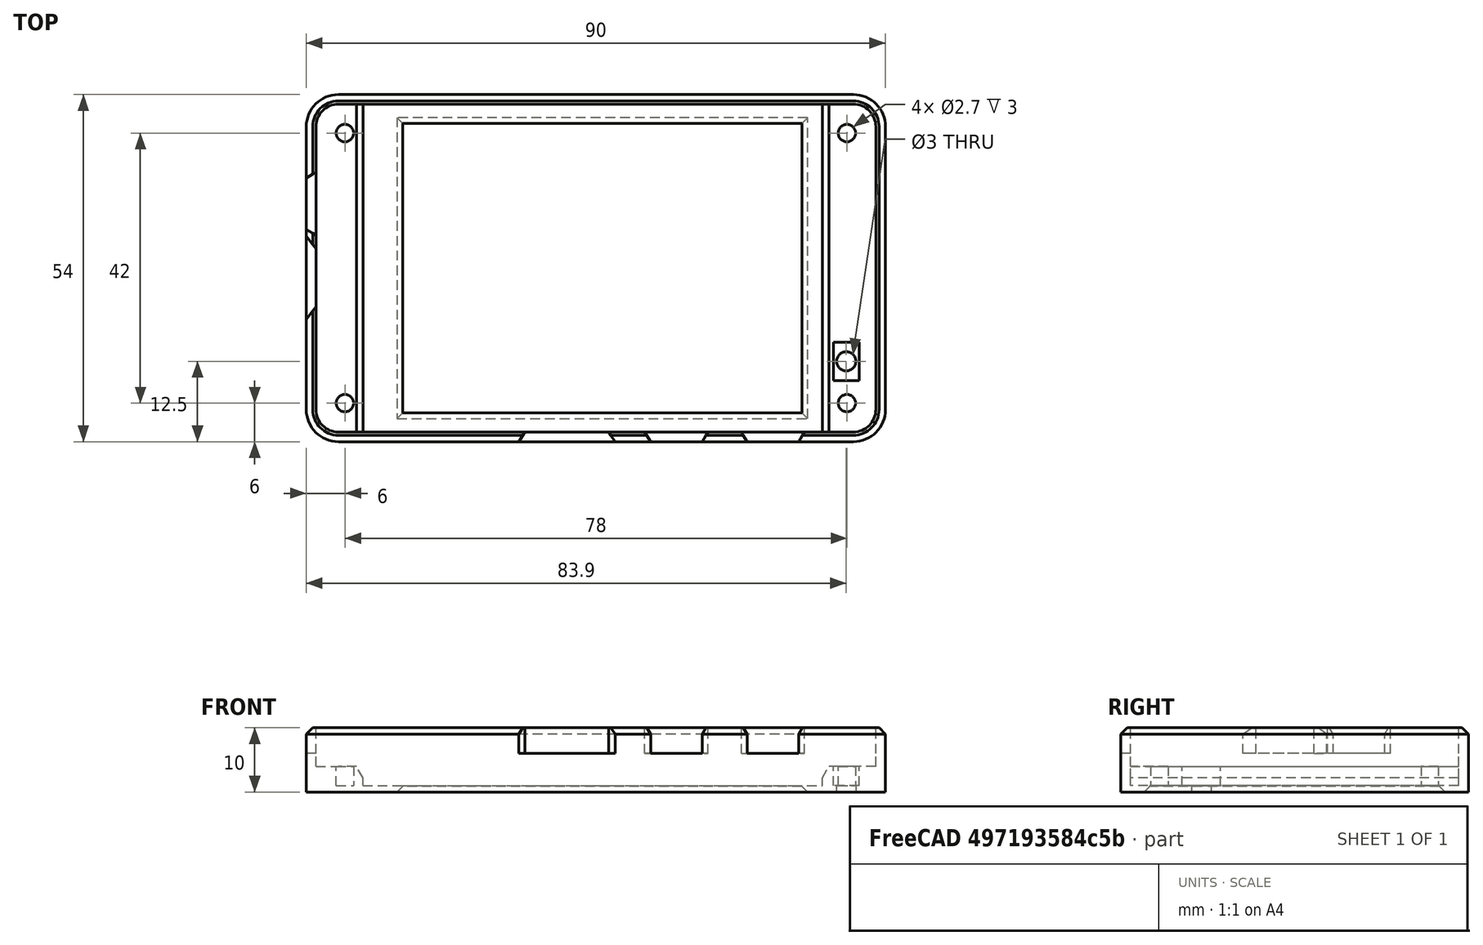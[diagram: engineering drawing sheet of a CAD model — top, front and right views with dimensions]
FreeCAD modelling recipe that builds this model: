
FCSTD DOCUMENT  (FreeCAD 0.21R33771 (Git))
Label: bezel_2432S028
License: All rights reserved
LicenseURL: http://en.wikipedia.org/wiki/All_rights_reserved
objects: Sketcher::SketchObject×5, Part::Extrusion×4, Part::Chamfer×3, Part::FeaturePython×1, Part::Mirroring×1, Mesh::Feature×1
note: 14 computed .brp shape members not serialized (recipe doc carries the construction recipe); baked Part::Feature solids carry a one-line shape summary decoded from their .brp

FEATURE [Sketcher::SketchObject] Sketch  label="Basis"
  FullyConstrained = true
  sketch-geometry (46):
    g0: ArcOfCircle CenterX=40 CenterY=22 CenterZ=0 NormalX=0 NormalY=0 NormalZ=1 AngleXU=0 Radius=3 StartAngle=5e-16 EndAngle=1.5708
    g1: LineSegment StartX=43 StartY=22 StartZ=0 EndX=43 EndY=-22 EndZ=0
    g2: ArcOfCircle CenterX=40 CenterY=-22 CenterZ=0 NormalX=0 NormalY=0 NormalZ=1 AngleXU=0 Radius=3 StartAngle=4.71239 EndAngle=6.28319
    g3: LineSegment StartX=40 StartY=-25 StartZ=0 EndX=-40 EndY=-25 EndZ=0
    g4: ArcOfCircle CenterX=-40 CenterY=-22 CenterZ=0 NormalX=0 NormalY=0 NormalZ=1 AngleXU=0 Radius=3 StartAngle=3.14159 EndAngle=4.71239
    g5: LineSegment StartX=-43 StartY=-22 StartZ=0 EndX=-43 EndY=22 EndZ=0
    g6: ArcOfCircle CenterX=-40 CenterY=22 CenterZ=0 NormalX=0 NormalY=0 NormalZ=1 AngleXU=0 Radius=3 StartAngle=1.5708 EndAngle=3.14159
    g7: LineSegment StartX=-40 StartY=25 StartZ=0 EndX=40 EndY=25 EndZ=0
    g8: GeomPoint X=43 Y=25 Z=0
    g9: GeomPoint X=-43 Y=-25 Z=0
    g10: Circle CenterX=-39 CenterY=21 CenterZ=0 NormalX=0 NormalY=0 NormalZ=1 AngleXU=0 Radius=1.6
    g11: Circle CenterX=-39 CenterY=-21 CenterZ=0 NormalX=0 NormalY=0 NormalZ=1 AngleXU=0 Radius=1.6
    g12: Circle CenterX=39 CenterY=21 CenterZ=0 NormalX=0 NormalY=0 NormalZ=1 AngleXU=0 Radius=1.6
    g13: Circle CenterX=39 CenterY=-21 CenterZ=0 NormalX=0 NormalY=0 NormalZ=1 AngleXU=0 Radius=1.6
    g14: LineSegment StartX=-35 StartY=25 StartZ=0 EndX=36 EndY=25 EndZ=0
    g15: LineSegment StartX=36 StartY=25 StartZ=0 EndX=36 EndY=-25 EndZ=0
    g16: LineSegment StartX=36 StartY=-25 StartZ=0 EndX=-35 EndY=-25 EndZ=0
    g17: LineSegment StartX=-35 StartY=-25 StartZ=0 EndX=-35 EndY=25 EndZ=0
    g18: LineSegment StartX=-40.4 StartY=-12 StartZ=0 EndX=-37.4 EndY=-12 EndZ=0
    g19: LineSegment StartX=-37.4 StartY=-12 StartZ=0 EndX=-37.4 EndY=-17 EndZ=0
    g20: LineSegment StartX=-37.4 StartY=-17 StartZ=0 EndX=-40.4 EndY=-17 EndZ=0
    g21: LineSegment StartX=-40.4 StartY=-17 StartZ=0 EndX=-40.4 EndY=-12 EndZ=0
    g22: LineSegment StartX=-2 StartY=-25 StartZ=0 EndX=11 EndY=-25 EndZ=0
    g23: LineSegment StartX=11 StartY=-25 StartZ=0 EndX=11 EndY=-28 EndZ=0
    g24: LineSegment StartX=11 StartY=-28 StartZ=0 EndX=-2 EndY=-28 EndZ=0
    g25: LineSegment StartX=-2 StartY=-28 StartZ=0 EndX=-2 EndY=-25 EndZ=0
    g26: LineSegment StartX=43 StartY=3 StartZ=0 EndX=53 EndY=3 EndZ=0
    g27: LineSegment StartX=53 StartY=3 StartZ=0 EndX=53 EndY=-6 EndZ=0
    g28: LineSegment StartX=53 StartY=-6 StartZ=0 EndX=43 EndY=-6 EndZ=0
    g29: LineSegment StartX=43 StartY=-6 StartZ=0 EndX=43 EndY=3 EndZ=0
    g30: LineSegment StartX=43 StartY=14 StartZ=0 EndX=45 EndY=14 EndZ=0
    g31: LineSegment StartX=45 StartY=14 StartZ=0 EndX=45 EndY=6 EndZ=0
    g32: LineSegment StartX=45 StartY=6 StartZ=0 EndX=43 EndY=6 EndZ=0
    g33: LineSegment StartX=43 StartY=6 StartZ=0 EndX=43 EndY=14 EndZ=0
    g34: LineSegment StartX=-31.5 StartY=-25 StartZ=0 EndX=-23.5 EndY=-25 EndZ=0
    g35: LineSegment StartX=-23.5 StartY=-25 StartZ=0 EndX=-23.5 EndY=-27 EndZ=0
    g36: LineSegment StartX=-23.5 StartY=-27 StartZ=0 EndX=-31.5 EndY=-27 EndZ=0
    g37: LineSegment StartX=-31.5 StartY=-27 StartZ=0 EndX=-31.5 EndY=-25 EndZ=0
    g38: LineSegment StartX=-16.5 StartY=-25 StartZ=0 EndX=-8.5 EndY=-25 EndZ=0
    g39: LineSegment StartX=-8.5 StartY=-25 StartZ=0 EndX=-8.5 EndY=-27 EndZ=0
    g40: LineSegment StartX=-8.5 StartY=-27 StartZ=0 EndX=-16.5 EndY=-27 EndZ=0
    g41: LineSegment StartX=-16.5 StartY=-27 StartZ=0 EndX=-16.5 EndY=-25 EndZ=0
    g42: LineSegment StartX=-32 StartY=22.5 StartZ=0 EndX=27 EndY=22.5 EndZ=0
    g43: LineSegment StartX=27 StartY=22.5 StartZ=0 EndX=27 EndY=-22.5 EndZ=0
    g44: LineSegment StartX=27 StartY=-22.5 StartZ=0 EndX=-32 EndY=-22.5 EndZ=0
    g45: LineSegment StartX=-32 StartY=-22.5 StartZ=0 EndX=-32 EndY=22.5 EndZ=0
  constraints (130):
    c: Tangent(g0,g1) = 1.5708
    c: Tangent(g1,g2) = 1.5708
    c: Tangent(g2,g3) = 1.5708
    c: Tangent(g3,g4) = 1.5708
    c: Tangent(g4,g5) = 1.5708
    c: Tangent(g5,g6) = 1.5708
    c: Tangent(g6,g7) = 1.5708
    c: Tangent(g7,g0) = 1.5708
    c: Horizontal(g3)
    c: Vertical(g1)
    c: Vertical(g5)
    c: Equal(g0,g2)
    c: Equal(g2,g4)
    c: Equal(g4,g6)
    c: PointOnObject(g8,g1)
    c: PointOnObject(g8,g7)
    c: PointOnObject(g9,g3)
    c: PointOnObject(g9,g5)
    c: DistanceY(g2,g0) = 50
    c: DistanceX(g5,g0) = 86
    c: Diameter(g0) = 6
    c: Symmetric(g6,g2,g-1)
    c: Horizontal(g7)
    c: Diameter(g10) = 3.2
    c: DistanceY(g10,g6) = 4
    c: DistanceX(g5,g10) = 4
    c: Equal(g10,g12)
    c: Horizontal(g10,g12)
    c: Vertical(g10,g11)
    c: Horizontal(g11,g13)
    c: Vertical(g13,g12)
    c: Equal(g10,g11)
    c: Equal(g11,g13)
    c: DistanceY(g2,g13) = 4
    c: DistanceX(g13,g1) = 4
    c: Coincident(g14,g15)
    c: Coincident(g15,g16)
    c: Coincident(g16,g17)
    c: Coincident(g17,g14)
    c: Horizontal(g14)
    c: Horizontal(g16)
    c: Vertical(g15)
    c: Vertical(g17)
    c: PointOnObject(g14,g7)
    c: PointOnObject(g16,g3)
    c: DistanceX(g14,g0) = 7
    c: DistanceX(g5,g14) = 8
    c: Coincident(g18,g19)
    c: Coincident(g19,g20)
    c: Coincident(g20,g21)
    c: Coincident(g21,g18)
    c: Horizontal(g18)
    c: Horizontal(g20)
    c: Vertical(g19)
    c: Vertical(g21)
    c: DistanceX(g20,g20) = 3
    c: DistanceY(g21,g21) = 5
    c: DistanceY(g3,g20) = 8
    c: DistanceX(g4,g20) = 2.6
    c: Coincident(g22,g23)
    c: Coincident(g23,g24)
    c: Coincident(g24,g25)
    c: Coincident(g25,g22)
    c: Horizontal(g22)
    c: Horizontal(g24)
    c: Vertical(g23)
    c: Vertical(g25)
    c: PointOnObject(g22,g3)
    c: DistanceX(g4,g22) = 41
    c: DistanceX(g22,g1) = 32
    c: DistanceY(g23,g23) = 3
    c: Coincident(g26,g27)
    c: Coincident(g27,g28)
    c: Coincident(g28,g29)
    c: Coincident(g29,g26)
    c: Horizontal(g26)
    c: Horizontal(g28)
    c: Vertical(g27)
    c: Vertical(g29)
    c: PointOnObject(g26,g1)
    c: DistanceY(g26,g0) = 22
    c: DistanceY(g2,g28) = 19
    c: DistanceX(g26,g26) = 10
    c: Coincident(g30,g31)
    c: Coincident(g31,g32)
    c: Coincident(g32,g33)
    c: Coincident(g33,g30)
    c: Horizontal(g30)
    c: Horizontal(g32)
    c: Vertical(g31)
    c: Vertical(g33)
    c: PointOnObject(g30,g1)
    c: DistanceY(g30,g0) = 11
    c: DistanceY(g2,g32) = 31
    c: DistanceX(g30,g30) = 2
    c: Coincident(g34,g35)
    c: Coincident(g35,g36)
    c: Coincident(g36,g37)
    c: Coincident(g37,g34)
    c: Horizontal(g34)
    c: Horizontal(g36)
    c: Vertical(g35)
    c: Vertical(g37)
    c: PointOnObject(g34,g3)
    c: Coincident(g38,g39)
    c: Coincident(g39,g40)
    c: Coincident(g40,g41)
    c: Coincident(g41,g38)
    c: Horizontal(g38)
    c: Horizontal(g40)
    c: Vertical(g39)
    c: Vertical(g41)
    c: PointOnObject(g38,g3)
    c: Equal(g31,g40)
    c: Equal(g40,g36)
    c: Equal(g32,g39)
    c: Equal(g39,g35)
    c: DistanceX(g4,g34) = 11.5
    c: DistanceX(g4,g38) = 26.5
    c: Coincident(g42,g43)
    c: Coincident(g43,g44)
    c: Coincident(g44,g45)
    c: Coincident(g45,g42)
    c: Horizontal(g42)
    c: Horizontal(g44)
    c: Vertical(g43)
    c: DistanceX(g44,g44) = 59
    c: DistanceY(g43,g43) = 45
    c: Symmetric(g42,g44,g-1)
    c: DistanceX(g14,g42) = 3
FEATURE [Sketcher::SketchObject] Sketch001
  ExternalGeometry = -> [Sketch]
  FullyConstrained = true
  Placement = pos=(0,0,4) rot=(0,0,1;0rad)
  sketch-geometry (20):
    g0: ArcOfCircle CenterX=-40 CenterY=22 CenterZ=0 NormalX=0 NormalY=0 NormalZ=1 AngleXU=0 Radius=3.5 StartAngle=1.5708 EndAngle=3.14159
    g1: LineSegment StartX=-40 StartY=25.5 StartZ=0 EndX=40 EndY=25.5 EndZ=0
    g2: ArcOfCircle CenterX=40 CenterY=22 CenterZ=0 NormalX=0 NormalY=0 NormalZ=1 AngleXU=0 Radius=3.5 StartAngle=4e-16 EndAngle=1.5708
    g3: LineSegment StartX=43.5 StartY=22 StartZ=0 EndX=43.5 EndY=-22 EndZ=0
    g4: ArcOfCircle CenterX=40 CenterY=-22 CenterZ=0 NormalX=0 NormalY=0 NormalZ=1 AngleXU=0 Radius=3.5 StartAngle=4.71239 EndAngle=6.28319
    g5: LineSegment StartX=40 StartY=-25.5 StartZ=0 EndX=-40 EndY=-25.5 EndZ=0
    g6: ArcOfCircle CenterX=-40 CenterY=-22 CenterZ=0 NormalX=0 NormalY=0 NormalZ=1 AngleXU=0 Radius=3.5 StartAngle=3.14159 EndAngle=4.71239
    g7: LineSegment StartX=-43.5 StartY=-22 StartZ=0 EndX=-43.5 EndY=22 EndZ=0
    g8: GeomPoint X=-43.5 Y=25.5 Z=0
    g9: GeomPoint X=43.5 Y=-25.5 Z=0
    g10: ArcOfCircle CenterX=-40 CenterY=22 CenterZ=0 NormalX=0 NormalY=0 NormalZ=1 AngleXU=0 Radius=5 StartAngle=1.5708 EndAngle=3.14159
    g11: LineSegment StartX=-40 StartY=27 StartZ=0 EndX=40 EndY=27 EndZ=0
    g12: ArcOfCircle CenterX=40 CenterY=22 CenterZ=0 NormalX=0 NormalY=0 NormalZ=1 AngleXU=0 Radius=5 StartAngle=0 EndAngle=1.5708
    g13: LineSegment StartX=45 StartY=22 StartZ=0 EndX=45 EndY=-22 EndZ=0
    g14: ArcOfCircle CenterX=40 CenterY=-22 CenterZ=0 NormalX=0 NormalY=0 NormalZ=1 AngleXU=0 Radius=5 StartAngle=4.71239 EndAngle=6.28319
    g15: LineSegment StartX=40 StartY=-27 StartZ=0 EndX=-40 EndY=-27 EndZ=0
    g16: ArcOfCircle CenterX=-40 CenterY=-22 CenterZ=0 NormalX=0 NormalY=0 NormalZ=1 AngleXU=0 Radius=5 StartAngle=3.14159 EndAngle=4.71239
    g17: LineSegment StartX=-45 StartY=-22 StartZ=0 EndX=-45 EndY=22 EndZ=0
    g18: GeomPoint X=-45 Y=27 Z=0
    g19: GeomPoint X=45 Y=-27 Z=0
  constraints (44):
    c: Tangent(g0,g1) = 1.5708
    c: Tangent(g1,g2) = 1.5708
    c: Tangent(g2,g3) = 1.5708
    c: Tangent(g3,g4) = 1.5708
    c: Tangent(g4,g5) = 1.5708
    c: Tangent(g5,g6) = 1.5708
    c: Tangent(g6,g7) = 1.5708
    c: Tangent(g7,g0) = 1.5708
    c: Horizontal(g1)
    c: Horizontal(g5)
    c: Vertical(g3)
    c: Vertical(g7)
    c: Equal(g0,g2)
    c: Equal(g2,g4)
    c: Equal(g4,g6)
    c: PointOnObject(g8,g1)
    c: PointOnObject(g8,g7)
    c: PointOnObject(g9,g3)
    c: PointOnObject(g9,g5)
    c: Coincident(g0,g-3)
    c: Coincident(g-4,g4)
    c: DistanceY(g-3,g0) = 0.5
    c: Tangent(g10,g11) = 1.5708
    c: Tangent(g11,g12) = 1.5708
    c: Tangent(g12,g13) = 1.5708
    c: Tangent(g13,g14) = 1.5708
    c: Tangent(g14,g15) = 1.5708
    c: Tangent(g15,g16) = 1.5708
    c: Tangent(g16,g17) = 1.5708
    c: Tangent(g17,g10) = 1.5708
    c: Horizontal(g11)
    c: Horizontal(g15)
    c: Vertical(g13)
    c: Vertical(g17)
    c: Equal(g10,g12)
    c: Equal(g12,g14)
    c: Equal(g14,g16)
    c: PointOnObject(g18,g11)
    c: PointOnObject(g18,g17)
    c: PointOnObject(g19,g13)
    c: PointOnObject(g19,g15)
    c: Coincident(g0,g10)
    c: Coincident(g4,g14)
    c: DistanceY(g-3,g10) = 2
FEATURE [Sketcher::SketchObject] Sketch002
  ExternalGeometry = -> [Sketch001,Sketch]
  FullyConstrained = true
  Placement = pos=(0,0,1) rot=(0,0,1;0rad)
  sketch-geometry (22):
    g0: ArcOfCircle CenterX=-40 CenterY=22 CenterZ=0 NormalX=0 NormalY=0 NormalZ=1 AngleXU=0 Radius=5 StartAngle=1.5708 EndAngle=3.14159
    g1: LineSegment StartX=-40 StartY=27 StartZ=0 EndX=40 EndY=27 EndZ=0
    g2: ArcOfCircle CenterX=40 CenterY=22 CenterZ=0 NormalX=0 NormalY=0 NormalZ=1 AngleXU=0 Radius=5 StartAngle=3e-16 EndAngle=1.5708
    g3: LineSegment StartX=45 StartY=22 StartZ=0 EndX=45 EndY=-22 EndZ=0
    g4: ArcOfCircle CenterX=40 CenterY=-22 CenterZ=0 NormalX=0 NormalY=0 NormalZ=1 AngleXU=0 Radius=5 StartAngle=4.71239 EndAngle=6.28319
    g5: LineSegment StartX=40 StartY=-27 StartZ=0 EndX=-40 EndY=-27 EndZ=0
    g6: ArcOfCircle CenterX=-40 CenterY=-22 CenterZ=0 NormalX=0 NormalY=0 NormalZ=1 AngleXU=0 Radius=5 StartAngle=3.14159 EndAngle=4.71239
    g7: LineSegment StartX=-45 StartY=-22 StartZ=0 EndX=-45 EndY=22 EndZ=0
    g8: GeomPoint X=-45 Y=27 Z=0
    g9: GeomPoint X=45 Y=-27 Z=0
    g10: LineSegment StartX=-35.2 StartY=25.5 StartZ=0 EndX=36.2 EndY=25.5 EndZ=0
    g11: LineSegment StartX=36.2 StartY=25.5 StartZ=0 EndX=36.2 EndY=-25.5 EndZ=0
    g12: LineSegment StartX=36.2 StartY=-25.5 StartZ=0 EndX=-35.2 EndY=-25.5 EndZ=0
    g13: LineSegment StartX=-35.2 StartY=-25.5 StartZ=0 EndX=-35.2 EndY=25.5 EndZ=0
    g14: Circle CenterX=-39 CenterY=21 CenterZ=0 NormalX=0 NormalY=0 NormalZ=1 AngleXU=0 Radius=1.35
    g15: Circle CenterX=-39 CenterY=-21 CenterZ=0 NormalX=0 NormalY=0 NormalZ=1 AngleXU=0 Radius=1.35
    g16: Circle CenterX=39 CenterY=-21 CenterZ=0 NormalX=0 NormalY=0 NormalZ=1 AngleXU=0 Radius=1.35
    g17: Circle CenterX=39 CenterY=21 CenterZ=0 NormalX=0 NormalY=0 NormalZ=1 AngleXU=0 Radius=1.35
    g18: LineSegment StartX=-40.9 StartY=-11.5 StartZ=0 EndX=-36.9 EndY=-11.5 EndZ=0
    g19: LineSegment StartX=-36.9 StartY=-11.5 StartZ=0 EndX=-36.9 EndY=-17.5 EndZ=0
    g20: LineSegment StartX=-36.9 StartY=-17.5 StartZ=0 EndX=-40.9 EndY=-17.5 EndZ=0
    g21: LineSegment StartX=-40.9 StartY=-17.5 StartZ=0 EndX=-40.9 EndY=-11.5 EndZ=0
  constraints (52):
    c: Tangent(g0,g1) = 1.5708
    c: Tangent(g1,g2) = 1.5708
    c: Tangent(g2,g3) = 1.5708
    c: Tangent(g3,g4) = 1.5708
    c: Tangent(g4,g5) = 1.5708
    c: Tangent(g5,g6) = 1.5708
    c: Tangent(g6,g7) = 1.5708
    c: Tangent(g7,g0) = 1.5708
    c: Horizontal(g5)
    c: Vertical(g3)
    c: Vertical(g7)
    c: Equal(g0,g2)
    c: Equal(g2,g4)
    c: Equal(g4,g6)
    c: PointOnObject(g8,g1)
    c: PointOnObject(g8,g7)
    c: PointOnObject(g9,g3)
    c: PointOnObject(g9,g5)
    c: Coincident(g-4,g4)
    c: Coincident(g0,g-3)
    c: Coincident(g0,g-3)
    c: Coincident(g10,g11)
    c: Coincident(g11,g12)
    c: Coincident(g12,g13)
    c: Coincident(g13,g10)
    c: Horizontal(g10)
    c: Horizontal(g12)
    c: Vertical(g11)
    c: PointOnObject(g10,g-7)
    c: DistanceX(g10,g-5) = 0.2
    c: DistanceX(g-6,g10) = 0.2
    c: Symmetric(g10,g12,g-1)
    c: Coincident(g14,g-8)
    c: Coincident(g15,g-9)
    c: Coincident(g16,g-11)
    c: Coincident(g17,g-10)
    c: Equal(g15,g14)
    c: Equal(g14,g17)
    c: Equal(g17,g16)
    c: Diameter(g14) = 2.7
    c: Coincident(g18,g19)
    c: Coincident(g19,g20)
    c: Coincident(g20,g21)
    c: Coincident(g21,g18)
    c: Horizontal(g18)
    c: Horizontal(g20)
    c: Vertical(g19)
    c: Vertical(g21)
    c: DistanceY(g-12,g18) = 0.5
    c: DistanceX(g18,g-12) = 0.5
    c: DistanceY(g20,g-13) = 0.5
    c: DistanceX(g-13,g19) = 0.5
FEATURE [Sketcher::SketchObject] Sketch003
  ExternalGeometry = -> [Sketch001,Sketch]
  FullyConstrained = true
  sketch-geometry (18):
    g0: LineSegment StartX=-32 StartY=22.5 StartZ=0 EndX=30 EndY=22.5 EndZ=0
    g1: LineSegment StartX=30 StartY=22.5 StartZ=0 EndX=30 EndY=-22.5 EndZ=0
    g2: LineSegment StartX=30 StartY=-22.5 StartZ=0 EndX=-32 EndY=-22.5 EndZ=0
    g3: LineSegment StartX=-32 StartY=-22.5 StartZ=0 EndX=-32 EndY=22.5 EndZ=0
    g4: ArcOfCircle CenterX=-40 CenterY=22 CenterZ=0 NormalX=0 NormalY=0 NormalZ=1 AngleXU=0 Radius=5 StartAngle=1.5708 EndAngle=3.14159
    g5: LineSegment StartX=-40 StartY=27 StartZ=0 EndX=40 EndY=27 EndZ=0
    g6: ArcOfCircle CenterX=40 CenterY=22 CenterZ=0 NormalX=0 NormalY=0 NormalZ=1 AngleXU=0 Radius=5 StartAngle=2e-16 EndAngle=1.5708
    g7: LineSegment StartX=45 StartY=22 StartZ=0 EndX=45 EndY=-22 EndZ=0
    g8: ArcOfCircle CenterX=40 CenterY=-22 CenterZ=0 NormalX=0 NormalY=0 NormalZ=1 AngleXU=0 Radius=5 StartAngle=4.71239 EndAngle=6.28319
    g9: LineSegment StartX=40 StartY=-27 StartZ=0 EndX=-40 EndY=-27 EndZ=0
    g10: ArcOfCircle CenterX=-40 CenterY=-22 CenterZ=0 NormalX=0 NormalY=0 NormalZ=1 AngleXU=0 Radius=5 StartAngle=3.14159 EndAngle=4.71239
    g11: LineSegment StartX=-45 StartY=-22 StartZ=0 EndX=-45 EndY=22 EndZ=0
    g12: GeomPoint X=-45 Y=27 Z=0
    g13: GeomPoint X=45 Y=-27 Z=0
    g14: Circle CenterX=-38.9 CenterY=-14.5 CenterZ=0 NormalX=0 NormalY=0 NormalZ=1 AngleXU=0 Radius=1.5
    g15: LineSegment StartX=-40.4 StartY=-12 StartZ=0 EndX=-37.4 EndY=-17 EndZ=0
    g16: LineSegment StartX=-40.4 StartY=-17 StartZ=0 EndX=-37.4 EndY=-12 EndZ=0
    g17: GeomPoint X=32 Y=22.5 Z=0
  constraints (39):
    c: Coincident(g0,g1)
    c: Coincident(g1,g2)
    c: Coincident(g2,g3)
    c: Coincident(g3,g0)
    c: Horizontal(g2)
    c: Vertical(g1)
    c: Coincident(g0,g-5)
    c: Tangent(g4,g5) = 1.5708
    c: Tangent(g5,g6) = 1.5708
    c: Tangent(g6,g7) = 1.5708
    c: Tangent(g7,g8) = 1.5708
    c: Tangent(g8,g9) = 1.5708
    c: Tangent(g9,g10) = 1.5708
    c: Tangent(g10,g11) = 1.5708
    c: Tangent(g11,g4) = 1.5708
    c: Horizontal(g9)
    c: Vertical(g7)
    c: Vertical(g11)
    c: Equal(g4,g6)
    c: Equal(g6,g8)
    c: Equal(g8,g10)
    c: PointOnObject(g12,g5)
    c: PointOnObject(g12,g11)
    c: PointOnObject(g13,g7)
    c: PointOnObject(g13,g9)
    c: Coincident(g8,g-4)
    c: Coincident(g4,g-3)
    c: Coincident(g-3,g4)
    c: Coincident(g15,g-7)
    c: PointOnObject(g14,g15)
    c: Coincident(g16,g-7)
    c: Coincident(g16,g-8)
    c: PointOnObject(g14,g16)
    c: Coincident(g15,g-8)
    c: Diameter(g14) = 3
    c: Coincident(g2,g-5)
    c: Symmetric(g17,g0,g-2)
    c: Horizontal(g0)
    c: DistanceX(g0,g17) = 2
FEATURE [Part::Extrusion] Extrude
  Base = -> Sketch003
  Dir = (0,0,1)
  DirMode = 2
  FaceMakerClass = Part::FaceMakerBullseye
  LengthFwd = 1
  LengthRev = 0
  Solid = true
  Symmetric = false
FEATURE [Part::Extrusion] Extrude001
  Base = -> Sketch002
  Dir = (0,0,1)
  DirMode = 2
  FaceMakerClass = Part::FaceMakerBullseye
  LengthFwd = 3
  LengthRev = 0
  Solid = true
  Symmetric = false
FEATURE [Part::Extrusion] Extrude002
  Base = -> Sketch001
  Dir = (0,0,1)
  DirMode = 2
  FaceMakerClass = Part::FaceMakerBullseye
  LengthFwd = 2
  LengthRev = 0
  Solid = true
  Symmetric = false
FEATURE [Sketcher::SketchObject] Sketch004
  ExternalGeometry = -> [Sketch001,Sketch]
  FullyConstrained = true
  Placement = pos=(0,0,6) rot=(0,0,1;0rad)
  sketch-geometry (49):
    g0: ArcOfCircle CenterX=-40 CenterY=22 CenterZ=0 NormalX=0 NormalY=0 NormalZ=1 AngleXU=0 Radius=5 StartAngle=1.5708 EndAngle=3.14159
    g1: LineSegment StartX=-40 StartY=27 StartZ=0 EndX=40 EndY=27 EndZ=0
    g2: ArcOfCircle CenterX=40 CenterY=22 CenterZ=0 NormalX=0 NormalY=0 NormalZ=1 AngleXU=0 Radius=5 StartAngle=0 EndAngle=1.5708
    g3: ArcOfCircle CenterX=40 CenterY=-22 CenterZ=0 NormalX=0 NormalY=0 NormalZ=1 AngleXU=0 Radius=5 StartAngle=4.71239 EndAngle=6.28319
    g4: ArcOfCircle CenterX=-40 CenterY=-22 CenterZ=0 NormalX=0 NormalY=0 NormalZ=1 AngleXU=0 Radius=5 StartAngle=3.14159 EndAngle=4.71239
    g5: LineSegment StartX=-45 StartY=-22 StartZ=0 EndX=-45 EndY=22 EndZ=0
    g6: GeomPoint X=-45 Y=27 Z=0
    g7: GeomPoint X=45 Y=-27 Z=0
    g8: LineSegment StartX=40 StartY=-27 StartZ=0 EndX=12 EndY=-27 EndZ=0
    g9: LineSegment StartX=12 StartY=-27 StartZ=0 EndX=-3 EndY=-27 EndZ=0
    g10: LineSegment StartX=45 StartY=5 StartZ=0 EndX=45 EndY=-8 EndZ=0
    g11: LineSegment StartX=45 StartY=-8 StartZ=0 EndX=45 EndY=-22 EndZ=0
    g12: ArcOfCircle CenterX=-40 CenterY=22 CenterZ=0 NormalX=0 NormalY=0 NormalZ=1 AngleXU=0 Radius=3.5 StartAngle=1.5708 EndAngle=3.14159
    g13: LineSegment StartX=-40 StartY=25.5 StartZ=0 EndX=40 EndY=25.5 EndZ=0
    g14: ArcOfCircle CenterX=40 CenterY=22 CenterZ=0 NormalX=0 NormalY=0 NormalZ=1 AngleXU=0 Radius=3.5 StartAngle=-2.7e-15 EndAngle=1.5708
    g15: ArcOfCircle CenterX=40 CenterY=-22 CenterZ=0 NormalX=0 NormalY=0 NormalZ=1 AngleXU=0 Radius=3.5 StartAngle=4.71239 EndAngle=6.28319
    g16: ArcOfCircle CenterX=-40 CenterY=-22 CenterZ=0 NormalX=0 NormalY=0 NormalZ=1 AngleXU=0 Radius=3.5 StartAngle=3.14159 EndAngle=4.71239
    g17: LineSegment StartX=-43.5 StartY=-22 StartZ=0 EndX=-43.5 EndY=22 EndZ=0
    g18: GeomPoint X=-43.5 Y=25.5 Z=0
    g19: GeomPoint X=43.5 Y=-25.5 Z=0
    g20: LineSegment StartX=40 StartY=-25.5 StartZ=0 EndX=11 EndY=-25.5 EndZ=0
    g21: LineSegment StartX=11 StartY=-25.5 StartZ=0 EndX=-2 EndY=-25.5 EndZ=0
    g22: LineSegment StartX=11 StartY=-25.5 StartZ=0 EndX=12 EndY=-27 EndZ=0
    g23: LineSegment StartX=-2 StartY=-25.5 StartZ=0 EndX=-3 EndY=-27 EndZ=0
    g24: LineSegment StartX=43.5 StartY=3 StartZ=0 EndX=43.5 EndY=-6 EndZ=0
    g25: LineSegment StartX=43.5 StartY=-6 StartZ=0 EndX=43.5 EndY=-22 EndZ=0
    g26: LineSegment StartX=43.5 StartY=3 StartZ=0 EndX=45 EndY=5 EndZ=0
    g27: LineSegment StartX=43.5 StartY=-6 StartZ=0 EndX=45 EndY=-8 EndZ=0
    g28: LineSegment StartX=43.5 StartY=22 StartZ=0 EndX=43.5 EndY=14.9 EndZ=0
    g29: LineSegment StartX=43.5 StartY=5.1 StartZ=0 EndX=43.5 EndY=3 EndZ=0
    g30: LineSegment StartX=43.5 StartY=14.9 StartZ=0 EndX=45 EndY=14 EndZ=0
    g31: LineSegment StartX=45 StartY=6 StartZ=0 EndX=43.5 EndY=5.1 EndZ=0
    g32: LineSegment StartX=45 StartY=22 StartZ=0 EndX=45 EndY=14 EndZ=0
    g33: LineSegment StartX=45 StartY=14 StartZ=0 EndX=45 EndY=6 EndZ=0
    g34: LineSegment StartX=45 StartY=6 StartZ=0 EndX=45 EndY=5 EndZ=0
    g35: LineSegment StartX=-32.4 StartY=-25.5 StartZ=0 EndX=-40 EndY=-25.5 EndZ=0
    g36: LineSegment StartX=-22.6 StartY=-25.5 StartZ=0 EndX=-32.4 EndY=-25.5 EndZ=0
    g37: LineSegment StartX=-31.5 StartY=-27 StartZ=0 EndX=-40 EndY=-27 EndZ=0
    g38: LineSegment StartX=-23.5 StartY=-27 StartZ=0 EndX=-31.5 EndY=-27 EndZ=0
    g39: LineSegment StartX=-32.4 StartY=-25.5 StartZ=0 EndX=-31.5 EndY=-27 EndZ=0
    g40: LineSegment StartX=-22.6 StartY=-25.5 StartZ=0 EndX=-23.5 EndY=-27 EndZ=0
    g41: LineSegment StartX=-17.4 StartY=-25.5 StartZ=0 EndX=-22.6 EndY=-25.5 EndZ=0
    g42: LineSegment StartX=-16.5 StartY=-27 StartZ=0 EndX=-23.5 EndY=-27 EndZ=0
    g43: LineSegment StartX=-3 StartY=-27 StartZ=0 EndX=-8.5 EndY=-27 EndZ=0
    g44: LineSegment StartX=-8.5 StartY=-27 StartZ=0 EndX=-16.5 EndY=-27 EndZ=0
    g45: LineSegment StartX=-2 StartY=-25.5 StartZ=0 EndX=-7.6 EndY=-25.5 EndZ=0
    g46: LineSegment StartX=-7.6 StartY=-25.5 StartZ=0 EndX=-17.4 EndY=-25.5 EndZ=0
    g47: LineSegment StartX=-17.4 StartY=-25.5 StartZ=0 EndX=-16.5 EndY=-27 EndZ=0
    g48: LineSegment StartX=-8.5 StartY=-27 StartZ=0 EndX=-7.6 EndY=-25.5 EndZ=0
  constraints (123):
    c: Tangent(g0,g1) = 1.5708
    c: Tangent(g1,g2) = 1.5708
    c: Coincident(g2,g32) = 1.5708
    c: Coincident(g11,g3) = 1.5708
    c: Coincident(g3,g8) = 1.5708
    c: Coincident(g37,g4) = 1.5708
    c: Tangent(g4,g5) = 1.5708
    c: Tangent(g5,g0) = 1.5708
    c: Vertical(g5)
    c: Equal(g0,g2)
    c: Equal(g3,g4)
    c: PointOnObject(g6,g1)
    c: PointOnObject(g6,g5)
    c: Coincident(g0,g-4)
    c: Coincident(g3,g-6)
    c: Coincident(g-3,g0)
    c: Coincident(g9,g43)
    c: Coincident(g8,g9)
    c: Horizontal(g8)
    c: Horizontal(g9)
    c: PointOnObject(g7,g8)
    c: Coincident(g3,g-6)
    c: Vertical(g4,g4)
    c: Coincident(g34,g10)
    c: Coincident(g10,g11)
    c: Vertical(g10)
    c: Vertical(g11)
    c: Horizontal(g2,g2)
    c: Horizontal(g11,g-6)
    c: Tangent(g12,g13) = 1.5708
    c: Tangent(g13,g14) = 1.5708
    c: Coincident(g14,g28) = 1.5708
    c: Coincident(g25,g15) = 1.5708
    c: Coincident(g15,g20) = 1.5708
    c: Coincident(g35,g16) = 1.5708
    c: Tangent(g16,g17) = 1.5708
    c: Tangent(g17,g12) = 1.5708
    c: Horizontal(g13)
    c: Vertical(g17)
    c: Equal(g12,g14)
    c: Equal(g14,g15)
    c: PointOnObject(g18,g13)
    c: PointOnObject(g18,g17)
    c: Coincident(g0,g12)
    c: Coincident(g15,g3)
    c: Coincident(g15,g-5)
    c: Coincident(g21,g45)
    c: Coincident(g20,g21)
    c: PointOnObject(g19,g20)
    c: Horizontal(g20)
    c: Coincident(g22,g20)
    c: Coincident(g22,g8)
    c: Coincident(g23,g45)
    c: Coincident(g23,g43)
    c: Coincident(g4,g16)
    c: Vertical(g16,g4)
    c: Coincident(g29,g24)
    c: Coincident(g24,g25)
    c: Vertical(g24)
    c: Vertical(g25)
    c: Coincident(g26,g29)
    c: Coincident(g26,g34)
    c: Coincident(g27,g25)
    c: Coincident(g27,g11)
    c: Horizontal(g25,g-5)
    c: Horizontal(g29,g-8)
    c: Horizontal(g25,g-8)
    c: DistanceY(g11,g25) = 2
    c: DistanceY(g26,g26) = 2
    c: Vertical(g45,g-7)
    c: Vertical(g20,g-7)
    c: DistanceX(g20,g8) = 1
    c: DistanceX(g43,g45) = 1
    c: Horizontal(g14,g2)
    c: Coincident(g28,g30)
    c: Vertical(g28)
    c: PointOnObject(g19,g28)
    c: Coincident(g31,g29)
    c: Vertical(g29)
    c: DistanceY(g30,g28) = 0.9
    c: DistanceY(g31,g31) = 0.9
    c: Vertical(g28,g29)
    c: Horizontal(g30,g-9)
    c: Horizontal(g31,g-9)
    c: Coincident(g32,g33)
    c: Vertical(g32)
    c: PointOnObject(g7,g32)
    c: Coincident(g33,g34)
    c: Vertical(g33)
    c: Vertical(g34)
    c: Coincident(g30,g32)
    c: Coincident(g31,g34)
    c: Coincident(g36,g35)
    c: Horizontal(g35)
    c: Coincident(g41,g36)
    c: Horizontal(g36)
    c: Coincident(g38,g37)
    c: Horizontal(g37)
    c: Coincident(g42,g38)
    c: Horizontal(g38)
    c: Coincident(g39,g35)
    c: Coincident(g39,g37)
    c: Coincident(g40,g41)
    c: Coincident(g40,g42)
    c: Vertical(g37,g-11)
    c: DistanceX(g35,g37) = 0.9
    c: Coincident(g42,g-11)
    c: Equal(g40,g39)
    c: Coincident(g46,g41)
    c: Horizontal(g41)
    c: Coincident(g44,g42)
    c: Coincident(g43,g44)
    c: Coincident(g45,g46)
    c: Horizontal(g45)
    c: Horizontal(g46)
    c: Coincident(g47,g41)
    c: Coincident(g47,g42)
    c: Coincident(g48,g43)
    c: Coincident(g48,g45)
    c: Coincident(g42,g-10)
    c: Coincident(g43,g-10)
    c: Equal(g40,g47)
    c: Equal(g47,g48)
FEATURE [Part::Extrusion] Extrude003
  Base = -> Sketch004
  Dir = (0,0,1)
  DirMode = 2
  FaceMakerClass = Part::FaceMakerBullseye
  LengthFwd = 4
  LengthRev = 0
  Solid = true
  Symmetric = false
FEATURE [Part::Chamfer] Chamfer
  Base = -> Extrude
  Edges = 4 edges r=0.9: [Edge27,Edge30,Edge33,Edge35]
FEATURE [Part::Chamfer] Chamfer001
  Base = -> Extrude003
  Edges = 5 edges r=1: [Edge7,Edge64,Edge79,Edge91,Edge103]
FEATURE [Part::Chamfer] Chamfer002
  Base = -> Extrude001
  Edges = 2 edges: [Edge31 r1=1.8 r2=1,Edge36 r1=1.8 r2=1]
FEATURE [Part::FeaturePython] Connect  # WARN: FeaturePython — macro-defined, semantics opaque (R4)
  Objects = -> [Extrude002,Chamfer002,Chamfer001,Chamfer]
  Tolerance = 0
FEATURE [Part::Mirroring] Mirror  label="Connect (gespiegelt)"
  Base = (0,0,0)
  Normal = (50,0,0)
  Source = -> Connect
FEATURE [Mesh::Feature] Mesh  label="Connect (gespiegelt) (Meshed)"
